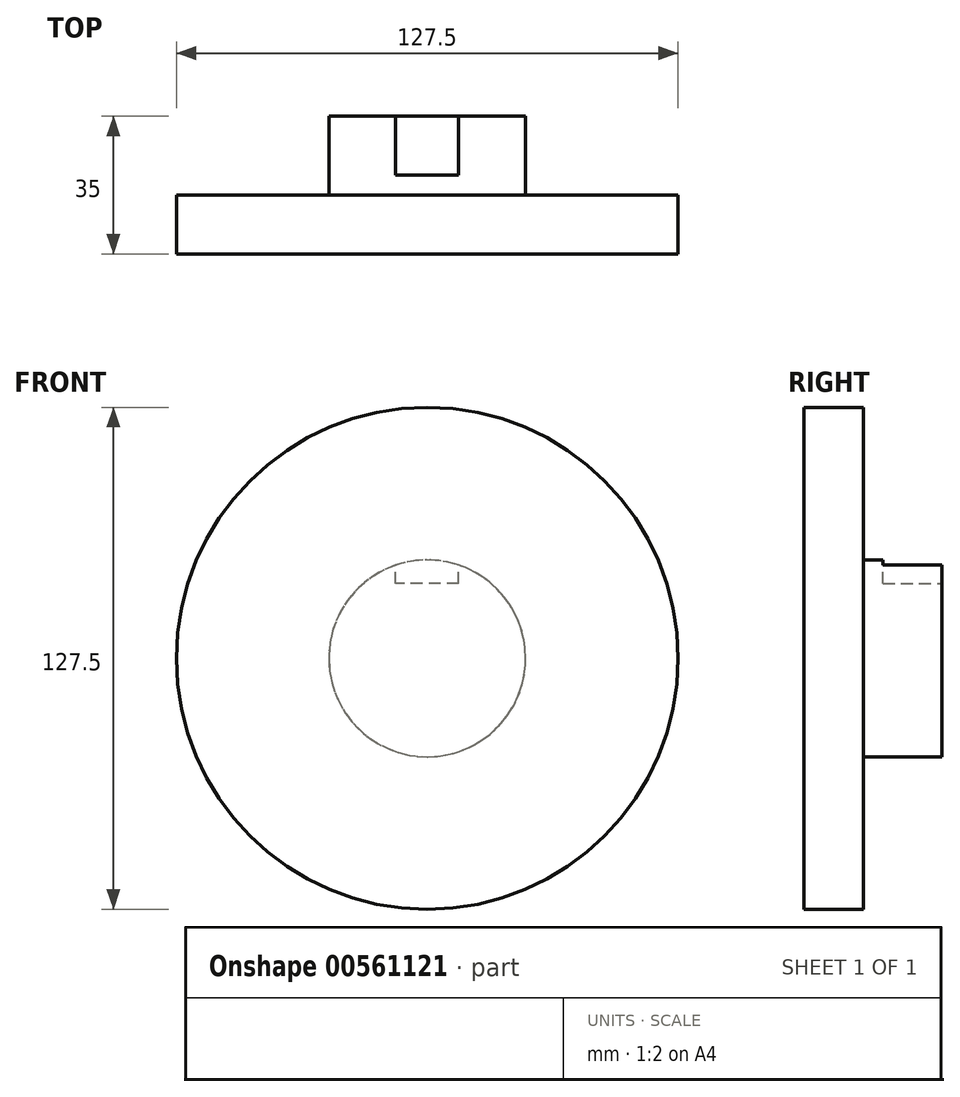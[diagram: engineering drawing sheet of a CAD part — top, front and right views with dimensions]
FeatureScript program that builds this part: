
annotation { "Feature Type Name" : "Feature", "Feature Type Description" : "" }
export const myFeature = defineFeature(function(context is Context, id is Id, definition is map)
    precondition{}
    {
        {
            var Q0;
            Q0=qCreatedBy(makeId("Front.planeOp"),FACE);
            var sketch = newSketch(context, id + "F0", { "sketchPlane" : qUnion([Q0])});
            skCircle(sketch, "E0", {"center": v(0, 0) * mm, "radius": 63.75 * mm});
            skCircle(sketch, "E1", {"center": v(0, 0) * mm, "radius": 70 * mm, "construction": true});
            skCircle(sketch, "E2", {"center": v(0, 0) * mm, "radius": 75 * mm, "construction": true});
            skLineSegment(sketch, "E3", {"start": v(0, 0) * mm, "end": v(0, 142.53) * mm, "construction": true});
            skLineSegment(sketch, "E4", {"start": v(0, 0) * mm, "end": v(-8.3, 147.71) * mm, "construction": true});
            skLineSegment(sketch, "E5", {"start": v(0, 70) * mm, "end": v(-109.9, 70) * mm, "construction": true});
            skLineSegment(sketch, "E6", {"start": v(0, 70) * mm, "end": v(-107.13, 31) * mm, "construction": true});
            skCircle(sketch, "E7", {"center": v(0, 0) * mm, "radius": 65.78 * mm, "construction": true});
            skCircle(sketch, "E8", {"center": v(0, 70) * mm, "radius": 17.5 * mm, "construction": true});
            skCircle(sketch, "E9", {"center": v(-16.33, 63.72) * mm, "radius": 17.5 * mm, "construction": true});
            skArc(sketch, "E10", {"start": v(-2.9, 74.94) * mm, "mid": v(0.11, 69.7) * mm, "end": v(1.17, 63.74) * mm});
            skArc(sketch, "E11.MirrorCS", {"start": v(-5.5, 74.8) * mm, "mid": v(-7.91, 69.25) * mm, "end": v(-8.3, 63.2) * mm});
            skArc(sketch, "E12", {"start": v(-5.5, 74.8) * mm, "mid": v(-4.2, 74.88) * mm, "end": v(-2.9, 74.94) * mm});
            skCircle(sketch, "E13", {"center": v(0, 0) * mm, "radius": 25 * mm});
            skSolve(sketch);
        }
        {
            var Q0;
            {var subQ0=sQuery(id+"F0.wireOp",EDGE,"E0");var subQ1=makeQuery(id+"F0.imprint","INTERSECT",VERTEX,{"derivedFrom":[subQ0,sQuery(id+"F0.wireOp",EDGE,"E10")]});Q0=makeQuery(id+"F0.imprint","IMPRINT",FACE,{"disambiguationData":[TD([[makeQuery(id+"F0.imprint","IMPRINT",EDGE,{"disambiguationData":[TD([[subQ1,-1.0]])],"derivedFrom":subQ0}),1.0]])]});}
            var Q1;
            {var subQ0=sQuery(id+"F0.wireOp",EDGE,"E10");Q1=makeQuery(id+"F0.imprint","IMPRINT",FACE,{"disambiguationData":[TD([[makeQuery(id+"F0.imprint","IMPRINT",EDGE,{"derivedFrom":subQ0}),-1.0]])]});}
            var Q2;
            Q2=makeQuery(id+"F0.imprint","IMPRINT",FACE,{"disambiguationData":[TD([[makeQuery(id+"F0.imprint","IMPRINT",EDGE,{"derivedFrom":sQuery(id+"F0.wireOp",EDGE,"E13")}),1.0]])]});
            extrude(context, id + "F1", {"entities" : qUnion([Q0, Q1, Q2]), "depth" : 15 * mm, "offsetDistance" : 25.4 * mm});
        }
        {
            var Q0;
            Q0=makeQuery(id+"F1.opExtrude","SWEPT_BODY",BODY,{"disambiguationData":[OSD([sQuery(id+"F0.wireOp",EDGE,"E0"),sQuery(id+"F0.wireOp",EDGE,"E10"),sQuery(id+"F0.wireOp",EDGE,"E11.MirrorCS"),sQuery(id+"F0.wireOp",EDGE,"E12")])]});
            var Q1;
            Q1=makeQuery(id+"F1.opExtrude","SWEPT_FACE",FACE,{"disambiguationData":[OSD([sQuery(id+"F0.wireOp",EDGE,"E0")])]});
            circularPattern(context, id + "F2", {"entities" : qUnion([Q0]), "axis" : qUnion([Q1]), "angle" : 360 * degree, "instanceCount" : 28, "equalSpace" : true});
        }
        {
            var Q0;
            Q0=makeQuery(id+"F0.imprint","IMPRINT",FACE,{"disambiguationData":[TD([[makeQuery(id+"F0.imprint","IMPRINT",EDGE,{"derivedFrom":sQuery(id+"F0.wireOp",EDGE,"E13")}),1.0]])]});
            extrude(context, id + "F3", {"entities" : qUnion([Q0]), "operationType" : NewBodyOperationType.ADD, "oppositeDirection" : true, "depth" : 20 * mm, "offsetDistance" : 25.4 * mm});
        }
        {
            var Q0;
            Q0=makeQuery(id+"F3.opExtrude","CAP_FACE",FACE,{"disambiguationData":[OSD([sQuery(id+"F0.wireOp",EDGE,"E13")])],"isStart":false});
            var sketch = newSketch(context, id + "F4", { "sketchPlane" : qUnion([Q0])});
            skLineSegment(sketch, "E14.bottom", {"start": v(-8, 19) * mm, "end": v(8, 19) * mm});
            skLineSegment(sketch, "E14.top", {"start": v(-8, 39.3) * mm, "end": v(8, 39.3) * mm});
            skLineSegment(sketch, "E14.left", {"start": v(-8, 19) * mm, "end": v(-8, 39.3) * mm});
            skLineSegment(sketch, "E14.right", {"start": v(8, 19) * mm, "end": v(8, 39.3) * mm});
            skSolve(sketch);
        }
        {
            var Q0;
            Q0 = qSketchRegion(id + "F4", true);
            extrude(context, id + "F5", {"entities" : qUnion([Q0]), "operationType" : NewBodyOperationType.REMOVE, "oppositeDirection" : true, "depth" : 15 * mm, "offsetDistance" : 25.4 * mm});
        }
    });
